# Revit family: Furniture_Table_Spacestor_6020-Fliptop-Rectangular
name_source: partatom
category: Furniture
revit_build: Autodesk Revit 2015 (Build: 20140223_1515(x64)
units: mm (PartAtom-declared; Revit-internal decimal feet)

## types (13) — shared parameters
Assembly Code = E2020200
Base Width = 450 mm  [stored 1.47638 ft]
Manufacturer = Spacestor
Spacestor White = Spacestor Table Top
URL = http://spacestor.uk.com

## per-type parameters (varying)
| type | Base Length | Canti Visi | Circular | Frame | Length | Osbourne Table Top | Polished Steel | Quadrant Frame | Quadrant Top | Rectangular | Semi-circular 1600 | Semi-circular 1800 | Trapezoidal | Width |
| Rectangular 1200w x 600d x 735h | 1070 mm  [stored 3.5105 ft] | No | No | Yes | 1200 mm | <By Category> | <By Category> | No | No | Yes | No | No | No | 600 mm  [stored 1.9685 ft] |
| Rectangular 1200w x 800d x 735h | 1070 mm  [stored 3.5105 ft] | No | No | Yes | 1200 mm | <By Category> | <By Category> | No | No | Yes | No | No | No | 800 mm  [stored 2.62467 ft] |
| Rectangular 1400w x 800d x 735h | 1070 mm  [stored 3.5105 ft] | No | No | Yes | 1400 mm | <By Category> | <By Category> | No | No | Yes | No | No | No | 800 mm  [stored 2.62467 ft] |
| Rectangular 1600w x 800d x 735h | 1070 mm  [stored 3.5105 ft] | No | No | Yes | 1600 mm  [stored 5.24934 ft] | <By Category> | <By Category> | No | No | Yes | No | No | No | 800 mm  [stored 2.62467 ft] |
| Rectangular 2000w x 800d x 735h | 1070 mm  [stored 3.5105 ft] | No | No | Yes | 2000 mm | <By Category> | <By Category> | No | No | Yes | No | No | No | 800 mm  [stored 2.62467 ft] |
| Square 800w x 800d x 735h | 620 mm  [stored 2.03412 ft] | No | No | Yes | 800 mm  [stored 2.62467 ft] | <By Category> | <By Category> | No | No | Yes | No | No | No | 800 mm  [stored 2.62467 ft] |
| Trapizoidal 1600w x 800/800d x 735h | 1070 mm  [stored 3.5105 ft] | Yes | No | Yes | 1200 mm | <By Category> | <By Category> | No | No | No | No | No | Yes | 800 mm  [stored 2.62467 ft] |
| Semi-circular 1600 DIA x 735h | 620 mm  [stored 2.03412 ft] | Yes | No | Yes | 1200 mm | Spacestor Table Top | Spacestor Polished Steel | No | No | No | Yes | No | No | 800 mm  [stored 2.62467 ft] |
| Semi-circular 1800 DIA x 735h | 620 mm  [stored 2.03412 ft] | Yes | No | Yes | 1200 mm | <By Category> | <By Category> | No | No | No | No | Yes | No | 800 mm  [stored 2.62467 ft] |
| Quadrant (top only) 800 DIA x 735h | 620 mm  [stored 2.03412 ft] | No | No | No | 1200 mm | <By Category> | <By Category> | No | Yes | No | No | No | No | 800 mm  [stored 2.62467 ft] |
| Quadrant (fixed frame) 800 DIA x 735h | 620 mm  [stored 2.03412 ft] | No | No | No | 1200 mm | <By Category> | <By Category> | Yes | Yes | No | No | No | No | 800 mm  [stored 2.62467 ft] |
| Circular 1000 DIA x 735h | 620 mm  [stored 2.03412 ft] | No | Yes | Yes | 1200 mm | <By Category> | <By Category> | No | No | No | No | No | No | 800 mm  [stored 2.62467 ft] |
| Rectangular 1800w x800d x 735h | 1070 mm  [stored 3.5105 ft] | No | No | Yes | 1800 mm  [stored 5.90551 ft] | <By Category> | <By Category> | No | No | Yes | No | No | No | 800 mm  [stored 2.62467 ft] |

note: [stored X ft] marks values corroborated as IEEE doubles in the binary element streams (Revit-internal decimal feet)

## geometry (parser evidence)
native form markers: Sweep x11
no freeform markers — native parametric forms only
